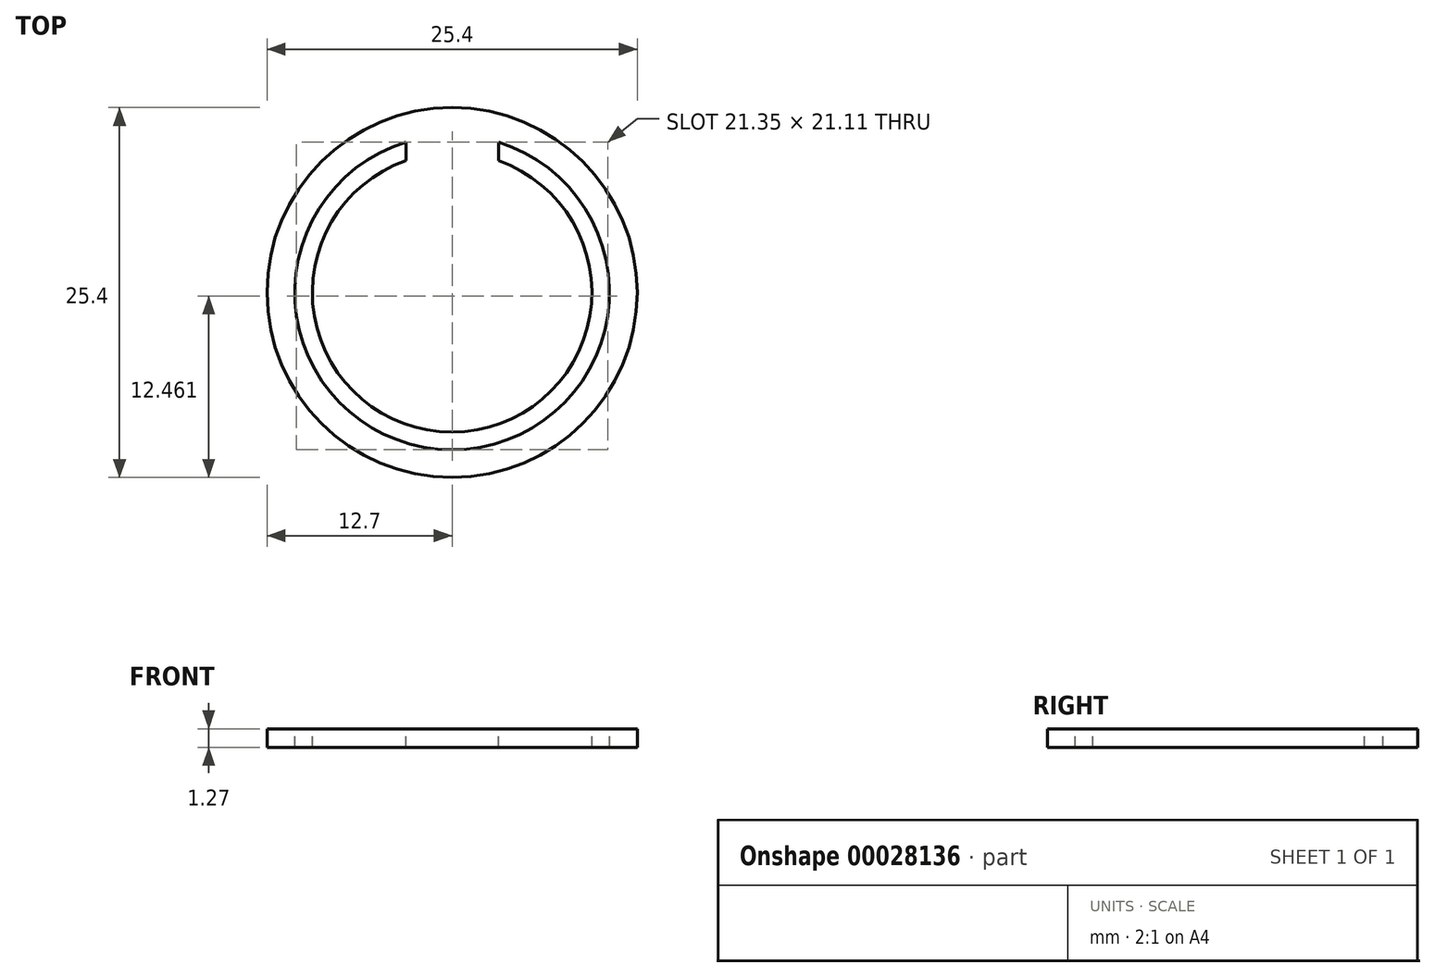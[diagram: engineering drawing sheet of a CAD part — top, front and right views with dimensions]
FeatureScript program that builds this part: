
annotation { "Feature Type Name" : "Feature", "Feature Type Description" : "" }
export const myFeature = defineFeature(function(context is Context, id is Id, definition is map)
    precondition{}
    {
        {
            var Q0;
            Q0=qCreatedBy(makeId("Top.planeOp"),FACE);
            var sketch = newSketch(context, id + "F0", { "sketchPlane" : qUnion([Q0])});
            skCircle(sketch, "E0", {"center": v(0, 0) * mm, "radius": 12.7 * mm});
            skSolve(sketch);
        }
        {
            var Q0;
            Q0=makeQuery(id+"F0.imprint","IMPRINT",FACE,{"disambiguationData":[TD([[makeQuery(id+"F0.imprint","IMPRINT",EDGE,{"derivedFrom":sQuery(id+"F0.wireOp",EDGE,"E0")}),1.0]])]});
            extrude(context, id + "F1", {"entities" : qUnion([Q0]), "depth" : 1.27 * mm});
        }
        {
            var Q0;
            Q0=makeQuery(id+"F1.opExtrude","CAP_FACE",FACE,{"disambiguationData":[OSD([sQuery(id+"F0.wireOp",EDGE,"E0")])],"isStart":false});
            var sketch = newSketch(context, id + "F2", { "sketchPlane" : qUnion([Q0])});
            skArc(sketch, "E1", {"start": v(-3.18, 10.32) * mm, "mid": v(0, -10.8) * mm, "end": v(3.18, 10.32) * mm});
            skArc(sketch, "E2", {"start": v(-3.18, 9.05) * mm, "mid": v(0, -9.59) * mm, "end": v(3.18, 9.05) * mm});
            skLineSegment(sketch, "E3", {"start": v(-3.18, 10.32) * mm, "end": v(-3.18, 9.05) * mm});
            skLineSegment(sketch, "E4", {"start": v(3.18, 10.32) * mm, "end": v(3.18, 9.05) * mm});
            skLineSegment(sketch, "E5", {"start": v(0, 0) * mm, "end": v(0, 33.36) * mm, "construction": true});
            skSolve(sketch);
        }
        {
            var Q0;
            Q0=makeQuery(id+"F2.imprint","IMPRINT",FACE,{"disambiguationData":[TD([[makeQuery(id+"F2.imprint","IMPRINT",EDGE,{"derivedFrom":sQuery(id+"F2.wireOp",EDGE,"E1")}),1.0]])]});
            extrude(context, id + "F3", {"entities" : qUnion([Q0]), "operationType" : NewBodyOperationType.REMOVE, "oppositeDirection" : true, "depth" : 25.4 * mm});
        }
    });
